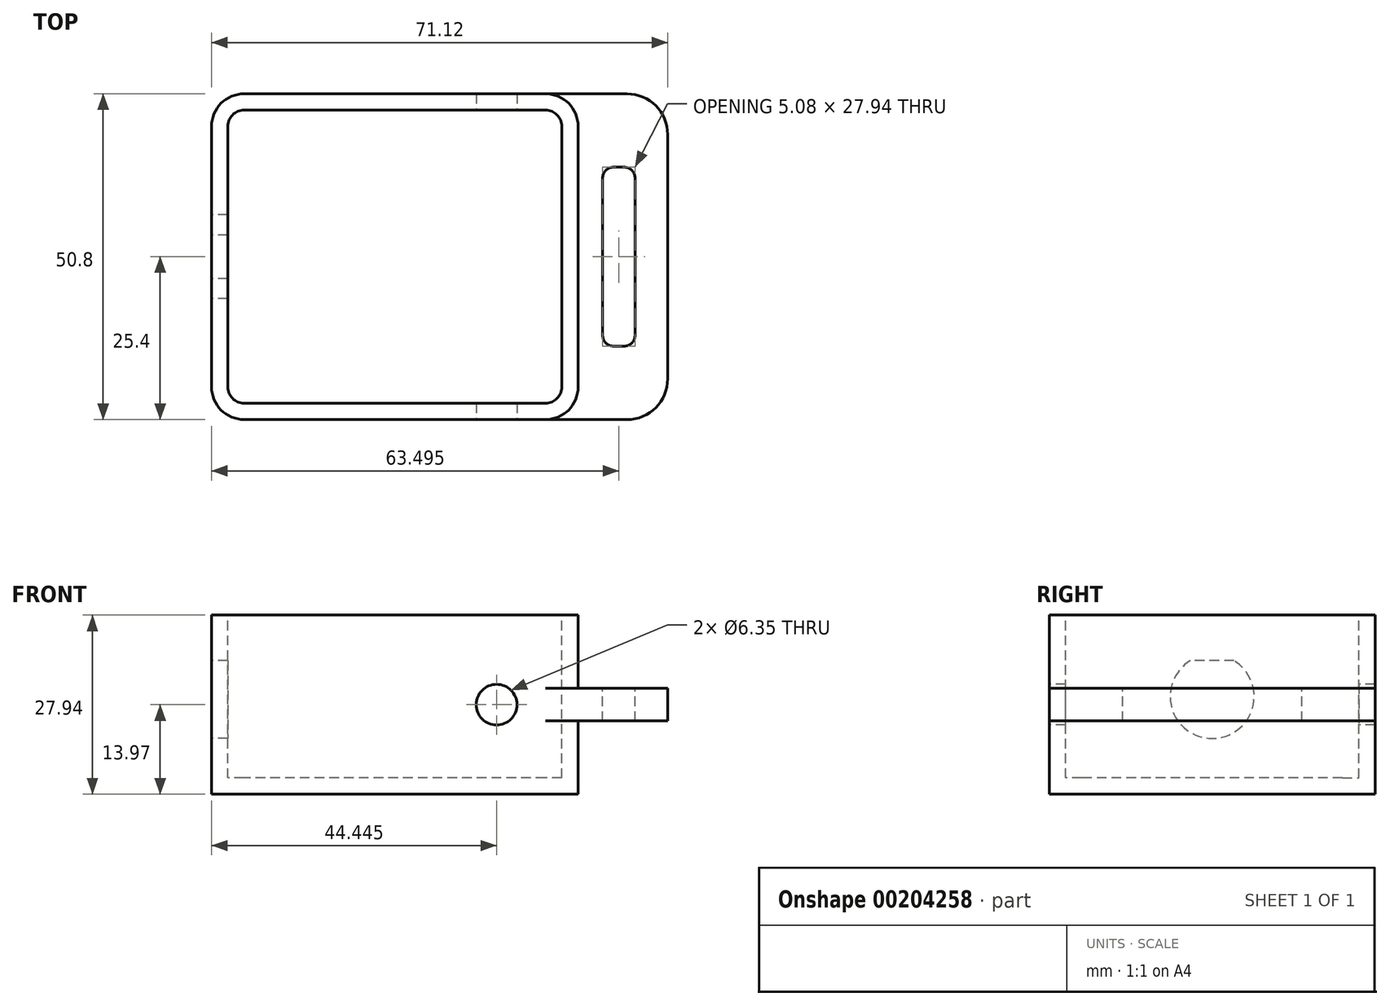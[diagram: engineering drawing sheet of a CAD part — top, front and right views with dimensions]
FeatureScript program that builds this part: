
annotation { "Feature Type Name" : "Feature", "Feature Type Description" : "" }
export const myFeature = defineFeature(function(context is Context, id is Id, definition is map)
    precondition{}
    {
        {
            var Q0;
            Q0=qCreatedBy(makeId("Top.planeOp"),FACE);
            var sketch = newSketch(context, id + "F0", { "sketchPlane" : qUnion([Q0])});
            skLineSegment(sketch, "E0.bottom", {"start": v(28.58, -25.4) * mm, "end": v(-28.58, -25.4) * mm});
            skLineSegment(sketch, "E0.top", {"start": v(28.58, 25.4) * mm, "end": v(-28.58, 25.4) * mm});
            skLineSegment(sketch, "E0.left", {"start": v(28.58, -25.4) * mm, "end": v(28.58, 25.4) * mm});
            skLineSegment(sketch, "E0.right", {"start": v(-28.58, -25.4) * mm, "end": v(-28.58, 25.4) * mm});
            skPoint(sketch, "E0.middle", {"position": v(0, 0) * mm});
            skSolve(sketch);
        }
        {
            var Q0;
            Q0 = qSketchRegion(id + "F0", true);
            extrude(context, id + "F1", {"entities" : qUnion([Q0]), "depth" : 27.94 * mm});
        }
        {
            var Q0;
            Q0=makeQuery(id+"F1.opExtrude","SWEPT_EDGE",EDGE,{"disambiguationData":[OSD([sQuery(id+"F0.wireOp",EDGE,"E0.top"),sQuery(id+"F0.wireOp",EDGE,"E0.right")])]});
            var Q1;
            Q1=makeQuery(id+"F1.opExtrude","SWEPT_EDGE",EDGE,{"disambiguationData":[OSD([sQuery(id+"F0.wireOp",EDGE,"E0.top"),sQuery(id+"F0.wireOp",EDGE,"E0.left")])]});
            var Q2;
            Q2=makeQuery(id+"F1.opExtrude","SWEPT_EDGE",EDGE,{"disambiguationData":[OSD([sQuery(id+"F0.wireOp",EDGE,"E0.bottom"),sQuery(id+"F0.wireOp",EDGE,"E0.left")])]});
            var Q3;
            Q3=makeQuery(id+"F1.opExtrude","SWEPT_EDGE",EDGE,{"disambiguationData":[OSD([sQuery(id+"F0.wireOp",EDGE,"E0.bottom"),sQuery(id+"F0.wireOp",EDGE,"E0.right")])]});
            fillet(context, id + "F2", {"entities" : qUnion([Q0, Q1, Q2, Q3]), "radius" : 5.08 * mm, "tangentPropagation" : true, "allowEdgeOverflow" : false});
        }
        {
            var Q0;
            Q0=makeQuery(id+"F1.opExtrude","CAP_FACE",FACE,{"disambiguationData":[OSD([sQuery(id+"F0.wireOp",EDGE,"E0.bottom"),sQuery(id+"F0.wireOp",EDGE,"E0.top"),sQuery(id+"F0.wireOp",EDGE,"E0.left"),sQuery(id+"F0.wireOp",EDGE,"E0.right")])],"isStart":true});
            cPlane(context, id + "F3", {"entities" : qUnion([Q0]), "cplaneType" : CPlaneType.OFFSET, "offset" : 13.97 * mm, "oppositeDirection" : true, "width" : 152.4 * mm, "height" : 152.4 * mm});
        }
        {
            var Q0;
            Q0=qCreatedBy(id+"F3.planeOp",FACE);
            var sketch = newSketch(context, id + "F4", { "sketchPlane" : qUnion([Q0])});
            skArc(sketch, "E1.0", {"start": v(28.58, 20.32) * mm, "mid": v(27.09, 23.91) * mm, "end": v(23.5, 25.4) * mm});
            skArc(sketch, "E2.0", {"start": v(23.5, -25.4) * mm, "mid": v(27.09, -23.91) * mm, "end": v(28.58, -20.32) * mm});
            skLineSegment(sketch, "E3.bottom", {"start": v(23.5, 25.4) * mm, "end": v(36.2, 25.4) * mm});
            skLineSegment(sketch, "E3.top", {"start": v(23.5, -25.4) * mm, "end": v(36.2, -25.4) * mm});
            skLineSegment(sketch, "E3.left", {"start": v(23.5, 25.4) * mm, "end": v(23.5, -25.4) * mm});
            skLineSegment(sketch, "E3.right", {"start": v(42.55, 19.05) * mm, "end": v(42.55, -19.05) * mm});
            skPoint(sketch, "E4.visualSharp", {"position": v(42.55, 25.4) * mm});
            skArc(sketch, "E4.filletArc", {"start": v(42.55, 19.05) * mm, "mid": v(40.69, 23.54) * mm, "end": v(36.2, 25.4) * mm});
            skPoint(sketch, "E5.visualSharp", {"position": v(42.55, -25.4) * mm});
            skArc(sketch, "E5.filletArc", {"start": v(36.2, -25.4) * mm, "mid": v(40.69, -23.54) * mm, "end": v(42.55, -19.05) * mm});
            skSolve(sketch);
        }
        {
            var Q0;
            Q0 = qSketchRegion(id + "F4", true);
            extrude(context, id + "F5", {"entities" : qUnion([Q0]), "operationType" : NewBodyOperationType.ADD, "endBound" : BoundingType.SYMMETRIC, "depth" : 5.08 * mm});
        }
        {
            var Q0;
            Q0=makeQuery(id+"F1.opExtrude","CAP_FACE",FACE,{"disambiguationData":[OSD([sQuery(id+"F0.wireOp",EDGE,"E0.bottom"),sQuery(id+"F0.wireOp",EDGE,"E0.top"),sQuery(id+"F0.wireOp",EDGE,"E0.left"),sQuery(id+"F0.wireOp",EDGE,"E0.right")])],"isStart":false});
            var sketch = newSketch(context, id + "F6", { "sketchPlane" : qUnion([Q0])});
            skLineSegment(sketch, "E6.0", {"start": v(-23.5, -22.86) * mm, "end": v(23.5, -22.86) * mm});
            skLineSegment(sketch, "E6.1", {"start": v(-26.04, 20.32) * mm, "end": v(-26.04, -20.32) * mm});
            skLineSegment(sketch, "E6.2", {"start": v(23.5, 22.86) * mm, "end": v(-23.5, 22.86) * mm});
            skLineSegment(sketch, "E6.3", {"start": v(26.04, -20.32) * mm, "end": v(26.04, 20.32) * mm});
            skPoint(sketch, "E7.visualSharp", {"position": v(-26.04, 22.86) * mm});
            skArc(sketch, "E7.filletArc", {"start": v(-23.5, 22.86) * mm, "mid": v(-25.3, 22.12) * mm, "end": v(-26.04, 20.32) * mm});
            skPoint(sketch, "E8.visualSharp", {"position": v(26.04, 22.86) * mm});
            skArc(sketch, "E8.filletArc", {"start": v(26.04, 20.32) * mm, "mid": v(25.3, 22.12) * mm, "end": v(23.5, 22.86) * mm});
            skPoint(sketch, "E9.visualSharp", {"position": v(26.04, -22.86) * mm});
            skArc(sketch, "E9.filletArc", {"start": v(23.5, -22.86) * mm, "mid": v(25.3, -22.12) * mm, "end": v(26.04, -20.32) * mm});
            skPoint(sketch, "E10.visualSharp", {"position": v(-26.04, -22.86) * mm});
            skArc(sketch, "E10.filletArc", {"start": v(-26.04, -20.32) * mm, "mid": v(-25.3, -22.12) * mm, "end": v(-23.5, -22.86) * mm});
            skSolve(sketch);
        }
        {
            var Q0;
            Q0 = qSketchRegion(id + "F6", true);
            extrude(context, id + "F7", {"entities" : qUnion([Q0]), "operationType" : NewBodyOperationType.REMOVE, "oppositeDirection" : true, "depth" : 25.4 * mm});
        }
        {
            var Q0;
            Q0=makeQuery(id+"F1.opExtrude","SWEPT_FACE",FACE,{"disambiguationData":[OSD([sQuery(id+"F0.wireOp",EDGE,"E0.right")])]});
            var sketch = newSketch(context, id + "F8", { "sketchPlane" : qUnion([Q0])});
            skPoint(sketch, "E11", {"position": v(0, 15.24) * mm});
            skCircle(sketch, "E12", {"center": v(0, 15.24) * mm, "radius": 6.54 * mm, "construction": true});
            skLineSegment(sketch, "E13", {"start": v(-3.4, 20.83) * mm, "end": v(3.4, 20.83) * mm});
            skArc(sketch, "E14", {"start": v(-3.4, 20.83) * mm, "mid": v(0, 8.7) * mm, "end": v(3.4, 20.83) * mm});
            skPoint(sketch, "E15.0", {"position": v(22.86, 2.54) * mm});
            skPoint(sketch, "E16.0", {"position": v(-22.86, 27.94) * mm});
            skLineSegment(sketch, "E17", {"start": v(-22.86, 27.94) * mm, "end": v(22.86, 2.54) * mm, "construction": true});
            skSolve(sketch);
        }
        {
            var Q0;
            Q0=makeQuery(id+"F8.imprint","IMPRINT",FACE,{"disambiguationData":[TD([[makeQuery(id+"F8.imprint","IMPRINT",EDGE,{"derivedFrom":sQuery(id+"F8.wireOp",EDGE,"E13")}),-1.0]])]});
            var Q1;
            Q1=makeQuery(id+"F7.boolean.opBoolean","COPY",FACE,{"derivedFrom":makeQuery(id+"F7.opExtrude","SWEPT_FACE",FACE,{"disambiguationData":[OSD([sQuery(id+"F6.wireOp",EDGE,"E6.1")])]})});
            extrude(context, id + "F9", {"entities" : qUnion([Q0]), "operationType" : NewBodyOperationType.REMOVE, "endBound" : BoundingType.UP_TO_SURFACE, "oppositeDirection" : true, "endBoundEntityFace" : qUnion([Q1]), "depth" : 25.4 * mm});
        }
        {
            var Q0;
            Q0=makeQuery(id+"FXWzee5nd5nYmyG_1.boolean.opBoolean","MERGE",FACE,{"derivedFrom":[makeQuery(id+"F1.opExtrude","SWEPT_FACE",FACE,{"disambiguationData":[OSD([sQuery(id+"F0.wireOp",EDGE,"E0.bottom")])]}),makeQuery(id+"FXWzee5nd5nYmyG_1.opExtrude","SWEPT_FACE",FACE,{"disambiguationData":[OSD([sQuery(id+"FCV9SzEZBoLJlct_1.wireOp",EDGE,"gKCvCpPp-IGvn-K7ZA-gIWn-0KwVQmQ5CGdc.bottom")])]})]});
            var sketch = newSketch(context, id + "F10", { "sketchPlane" : qUnion([Q0])});
            skLineSegment(sketch, "E18", {"start": v(-23.5, 13.97) * mm, "end": v(23.5, 13.97) * mm, "construction": true});
            skPoint(sketch, "E19", {"position": v(15.88, 13.97) * mm});
            skCircle(sketch, "E20", {"center": v(15.88, 13.97) * mm, "radius": 3.18 * mm});
            skSolve(sketch);
        }
        {
            var Q0;
            Q0=makeQuery(id+"F10.imprint","IMPRINT",FACE,{"disambiguationData":[TD([[makeQuery(id+"F10.imprint","IMPRINT",EDGE,{"derivedFrom":sQuery(id+"F10.wireOp",EDGE,"E20")}),1.0]])]});
            extrude(context, id + "F11", {"entities" : qUnion([Q0]), "operationType" : NewBodyOperationType.REMOVE, "endBound" : BoundingType.THROUGH_ALL, "oppositeDirection" : true, "depth" : 25.4 * mm});
        }
        {
            var Q0;
            Q0=makeQuery(id+"F5.opExtrude","CAP_FACE",FACE,{"disambiguationData":[OSD([sQuery(id+"F4.wireOp",EDGE,"E3.bottom"),sQuery(id+"F4.wireOp",EDGE,"E3.top"),sQuery(id+"F4.wireOp",EDGE,"E3.left"),sQuery(id+"F4.wireOp",EDGE,"E3.right"),sQuery(id+"F4.wireOp",EDGE,"E4.filletArc"),sQuery(id+"F4.wireOp",EDGE,"E5.filletArc")])],"isStart":true});
            var sketch = newSketch(context, id + "F12", { "sketchPlane" : qUnion([Q0])});
            skLineSegment(sketch, "E21.bottom", {"start": v(34.16, 13.97) * mm, "end": v(35.69, 13.97) * mm});
            skLineSegment(sketch, "E21.top", {"start": v(34.16, -13.97) * mm, "end": v(35.69, -13.97) * mm});
            skLineSegment(sketch, "E21.left", {"start": v(32.39, 12.2) * mm, "end": v(32.39, -12.2) * mm});
            skLineSegment(sketch, "E21.right", {"start": v(37.47, 12.2) * mm, "end": v(37.47, -12.2) * mm});
            skPoint(sketch, "E22", {"position": v(37.47, 0) * mm});
            skPoint(sketch, "E23.visualSharp", {"position": v(37.47, 13.97) * mm});
            skArc(sketch, "E23.filletArc", {"start": v(37.47, 12.2) * mm, "mid": v(36.94, 13.45) * mm, "end": v(35.69, 13.97) * mm});
            skPoint(sketch, "E24.visualSharp", {"position": v(32.39, 13.97) * mm});
            skArc(sketch, "E24.filletArc", {"start": v(34.16, 13.97) * mm, "mid": v(32.9, 13.45) * mm, "end": v(32.39, 12.2) * mm});
            skPoint(sketch, "E25.visualSharp", {"position": v(37.47, -13.97) * mm});
            skArc(sketch, "E25.filletArc", {"start": v(35.69, -13.97) * mm, "mid": v(36.94, -13.45) * mm, "end": v(37.47, -12.2) * mm});
            skPoint(sketch, "E26.visualSharp", {"position": v(32.39, -13.97) * mm});
            skArc(sketch, "E26.filletArc", {"start": v(32.39, -12.2) * mm, "mid": v(32.9, -13.45) * mm, "end": v(34.16, -13.97) * mm});
            skSolve(sketch);
        }
        {
            var Q0;
            Q0 = qSketchRegion(id + "F12", true);
            var Q1;
            Q1=makeQuery(id+"F5.opExtrude","CAP_FACE",FACE,{"disambiguationData":[OSD([sQuery(id+"F4.wireOp",EDGE,"E3.bottom"),sQuery(id+"F4.wireOp",EDGE,"E3.top"),sQuery(id+"F4.wireOp",EDGE,"E3.left"),sQuery(id+"F4.wireOp",EDGE,"E3.right"),sQuery(id+"F4.wireOp",EDGE,"E4.filletArc"),sQuery(id+"F4.wireOp",EDGE,"E5.filletArc")])],"isStart":false});
            extrude(context, id + "F13", {"entities" : qUnion([Q0]), "operationType" : NewBodyOperationType.REMOVE, "endBound" : BoundingType.UP_TO_SURFACE, "oppositeDirection" : true, "endBoundEntityFace" : qUnion([Q1]), "depth" : 25.4 * mm});
        }
    });
